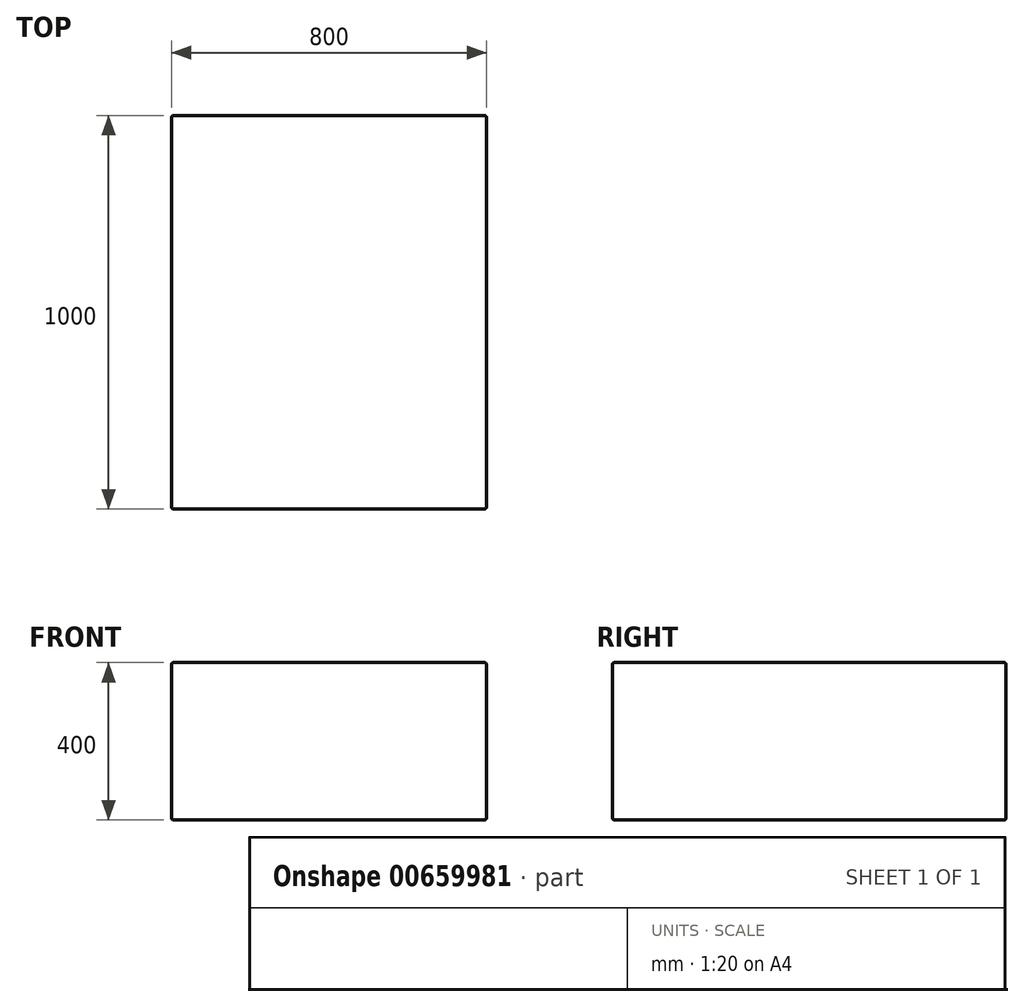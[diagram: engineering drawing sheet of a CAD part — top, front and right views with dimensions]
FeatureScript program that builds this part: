
annotation { "Feature Type Name" : "Feature", "Feature Type Description" : "" }
export const myFeature = defineFeature(function(context is Context, id is Id, definition is map)
    precondition{}
    {
        {
            var Q0;
            Q0=qCreatedBy(makeId("Top.planeOp"),FACE);
            var sketch = newSketch(context, id + "F0", { "sketchPlane" : qUnion([Q0])});
            skLineSegment(sketch, "E0.bottom", {"start": v(0, 0) * mm, "end": v(800, 0) * mm});
            skLineSegment(sketch, "E0.top", {"start": v(0, -1000) * mm, "end": v(800, -1000) * mm});
            skLineSegment(sketch, "E0.left", {"start": v(0, 0) * mm, "end": v(0, -1000) * mm});
            skLineSegment(sketch, "E0.right", {"start": v(800, 0) * mm, "end": v(800, -1000) * mm});
            skSolve(sketch);
        }
        {
            var Q0;
            Q0=makeQuery(id+"F0.imprint","IMPRINT",FACE,{"disambiguationData":[TD([[makeQuery(id+"F0.imprint","IMPRINT",EDGE,{"derivedFrom":sQuery(id+"F0.wireOp",EDGE,"E0.bottom")}),-1.0]])]});
            extrude(context, id + "F1", {"entities" : qUnion([Q0]), "depth" : 400 * mm, "offsetDistance" : 25 * mm});
        }
        {
            var Q0;
            Q0=makeQuery(id+"F1.opExtrude","CAP_FACE",FACE,{"disambiguationData":[OSD([sQuery(id+"F0.wireOp",EDGE,"E0.bottom"),sQuery(id+"F0.wireOp",EDGE,"E0.top"),sQuery(id+"F0.wireOp",EDGE,"E0.left"),sQuery(id+"F0.wireOp",EDGE,"E0.right")])],"isStart":false});
            var Q1;
            Q1=makeQuery(id+"F1.opExtrude","SWEPT_FACE",FACE,{"disambiguationData":[OSD([sQuery(id+"F0.wireOp",EDGE,"E0.right")])]});
            var Q2;
            Q2=makeQuery(id+"F1.opExtrude","SWEPT_FACE",FACE,{"disambiguationData":[OSD([sQuery(id+"F0.wireOp",EDGE,"E0.bottom")])]});
            var Q3;
            Q3=makeQuery(id+"F1.opExtrude","SWEPT_FACE",FACE,{"disambiguationData":[OSD([sQuery(id+"F0.wireOp",EDGE,"E0.left")])]});
            var Q4;
            Q4=makeQuery(id+"F1.opExtrude","CAP_FACE",FACE,{"disambiguationData":[OSD([sQuery(id+"F0.wireOp",EDGE,"E0.bottom"),sQuery(id+"F0.wireOp",EDGE,"E0.top"),sQuery(id+"F0.wireOp",EDGE,"E0.left"),sQuery(id+"F0.wireOp",EDGE,"E0.right")])],"isStart":true});
            var Q5;
            Q5=makeQuery(id+"F1.opExtrude","SWEPT_FACE",FACE,{"disambiguationData":[OSD([sQuery(id+"F0.wireOp",EDGE,"E0.top")])]});
            fillet(context, id + "F2", {"entities" : qUnion([Q0, Q1, Q2, Q3, Q4, Q5]), "radius" : 5 * mm, "tangentPropagation" : true, "allowEdgeOverflow" : false});
        }
    });
